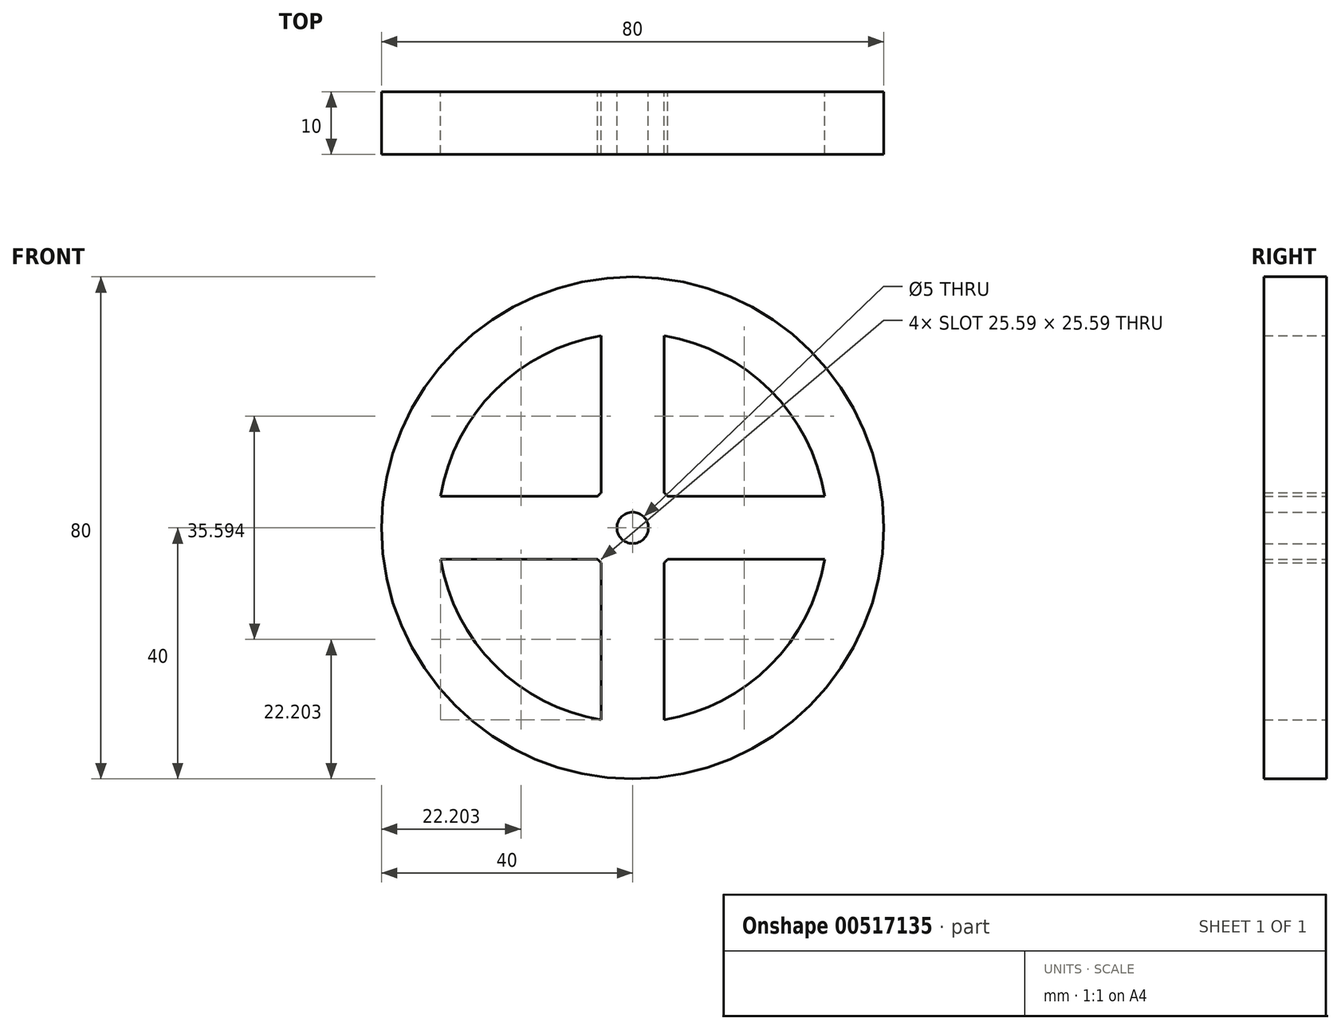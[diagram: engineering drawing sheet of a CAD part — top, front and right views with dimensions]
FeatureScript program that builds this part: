
annotation { "Feature Type Name" : "Feature", "Feature Type Description" : "" }
export const myFeature = defineFeature(function(context is Context, id is Id, definition is map)
    precondition{}
    {
        {
            var Q0;
            Q0=qCreatedBy(makeId("Front.planeOp"),FACE);
            var sketch = newSketch(context, id + "F0", { "sketchPlane" : qUnion([Q0])});
            skArc(sketch, "E0", {"start": v(-5, 5.6) * mm, "mid": v(-5.3, 5.3) * mm, "end": v(-5.6, 5) * mm});
            skCircle(sketch, "E1", {"center": v(0, 0) * mm, "radius": 2.5 * mm});
            skArc(sketch, "E2", {"start": v(-5, 30.6) * mm, "mid": v(-21.92, 21.92) * mm, "end": v(-30.6, 5) * mm});
            skCircle(sketch, "E3", {"center": v(0, 0) * mm, "radius": 40 * mm});
            skLineSegment(sketch, "E4.0", {"start": v(5, 5.6) * mm, "end": v(5, 30.6) * mm});
            skLineSegment(sketch, "E5.0", {"start": v(-5, 5.6) * mm, "end": v(-5, 30.6) * mm});
            skLineSegment(sketch, "E6.0", {"start": v(5.6, 5) * mm, "end": v(30.6, 5) * mm});
            skLineSegment(sketch, "E7.0", {"start": v(5.6, -5) * mm, "end": v(30.6, -5) * mm});
            skLineSegment(sketch, "E8.0", {"start": v(-5, -5.6) * mm, "end": v(-5, -30.6) * mm});
            skLineSegment(sketch, "E9.0", {"start": v(5, -5.6) * mm, "end": v(5, -30.6) * mm});
            skLineSegment(sketch, "E10.0", {"start": v(-5.6, 5) * mm, "end": v(-30.6, 5) * mm});
            skLineSegment(sketch, "E11.0", {"start": v(-5.6, -5) * mm, "end": v(-30.6, -5) * mm});
            skArc(sketch, "E12.trimOffspring", {"start": v(5.6, 5) * mm, "mid": v(5.3, 5.3) * mm, "end": v(5, 5.6) * mm});
            skArc(sketch, "E13.trimOffspring", {"start": v(5, -5.6) * mm, "mid": v(5.3, -5.3) * mm, "end": v(5.6, -5) * mm});
            skArc(sketch, "E14.trimOffspring", {"start": v(-5.6, -5) * mm, "mid": v(-5.3, -5.3) * mm, "end": v(-5, -5.6) * mm});
            skArc(sketch, "E15.trimOffspring", {"start": v(30.6, 5) * mm, "mid": v(21.92, 21.92) * mm, "end": v(5, 30.6) * mm});
            skArc(sketch, "E16.trimOffspring", {"start": v(-30.6, -5) * mm, "mid": v(-21.92, -21.92) * mm, "end": v(-5, -30.6) * mm});
            skArc(sketch, "E17.trimOffspring", {"start": v(5, -30.6) * mm, "mid": v(21.92, -21.92) * mm, "end": v(30.6, -5) * mm});
            skSolve(sketch);
        }
        {
            var Q0;
            Q0=makeQuery(id+"F0.imprint","IMPRINT",FACE,{"disambiguationData":[TD([[makeQuery(id+"F0.imprint","IMPRINT",EDGE,{"derivedFrom":sQuery(id+"F0.wireOp",EDGE,"E0")}),1.0]])]});
            extrude(context, id + "F1", {"entities" : qUnion([Q0]), "depth" : 10 * mm, "offsetDistance" : 25 * mm});
        }
    });
